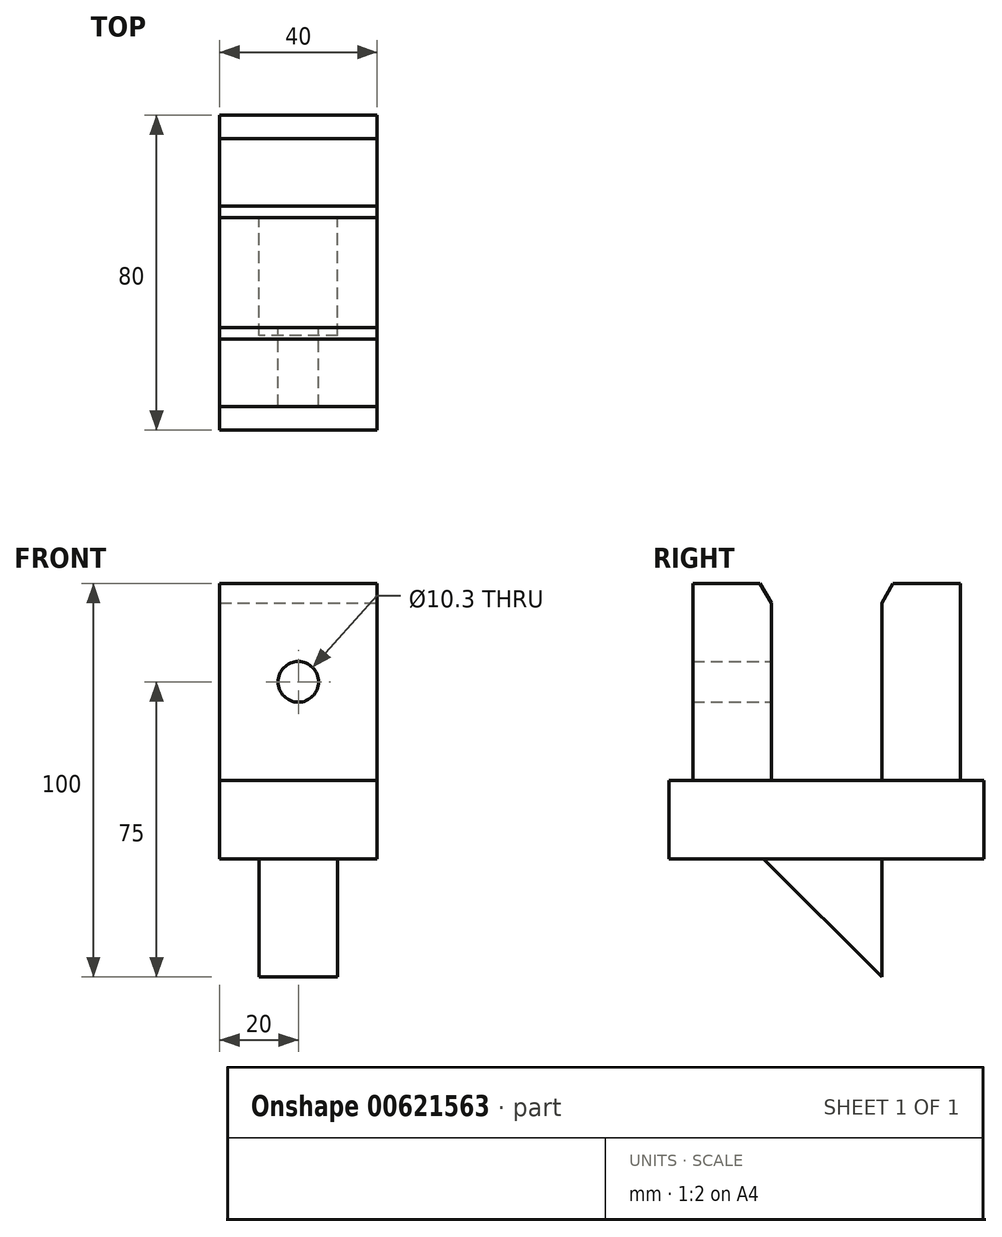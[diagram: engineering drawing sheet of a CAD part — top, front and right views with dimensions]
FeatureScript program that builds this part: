
annotation { "Feature Type Name" : "Feature", "Feature Type Description" : "" }
export const myFeature = defineFeature(function(context is Context, id is Id, definition is map)
    precondition{}
    {
        {
            var Q0;
            Q0=qCreatedBy(makeId("Top.planeOp"),FACE);
            var sketch = newSketch(context, id + "F0", { "sketchPlane" : qUnion([Q0])});
            skLineSegment(sketch, "E0.bottom", {"start": v(20, -40) * mm, "end": v(-20, -40) * mm});
            skLineSegment(sketch, "E0.top", {"start": v(20, 40) * mm, "end": v(-20, 40) * mm});
            skLineSegment(sketch, "E0.left", {"start": v(20, -40) * mm, "end": v(20, 40) * mm});
            skLineSegment(sketch, "E0.right", {"start": v(-20, -40) * mm, "end": v(-20, 40) * mm});
            skPoint(sketch, "E0.middle", {"position": v(0, 0) * mm});
            skSolve(sketch);
        }
        {
            var Q0;
            Q0 = qSketchRegion(id + "F0", true);
            extrude(context, id + "F1", {"entities" : qUnion([Q0]), "depth" : 20 * mm, "offsetDistance" : 25 * mm});
        }
        {
            var Q0;
            Q0=makeQuery(id+"F1.opExtrude","CAP_FACE",FACE,{"disambiguationData":[OSD([sQuery(id+"F0.wireOp",EDGE,"E0.bottom"),sQuery(id+"F0.wireOp",EDGE,"E0.top"),sQuery(id+"F0.wireOp",EDGE,"E0.left"),sQuery(id+"F0.wireOp",EDGE,"E0.right")])],"isStart":false});
            var sketch = newSketch(context, id + "F2", { "sketchPlane" : qUnion([Q0])});
            skLineSegment(sketch, "E1.bottom", {"start": v(20, -34) * mm, "end": v(-20, -34) * mm});
            skLineSegment(sketch, "E1.top", {"start": v(20, -14) * mm, "end": v(-20, -14) * mm});
            skLineSegment(sketch, "E1.left", {"start": v(20, -34) * mm, "end": v(20, -14) * mm});
            skLineSegment(sketch, "E1.right", {"start": v(-20, -34) * mm, "end": v(-20, -14) * mm});
            skPoint(sketch, "E1.middle", {"position": v(0, -24) * mm});
            skLineSegment(sketch, "E2.bottom", {"start": v(-20, 14) * mm, "end": v(20, 14) * mm});
            skLineSegment(sketch, "E2.top", {"start": v(-20, 34) * mm, "end": v(20, 34) * mm});
            skLineSegment(sketch, "E2.left", {"start": v(-20, 14) * mm, "end": v(-20, 34) * mm});
            skLineSegment(sketch, "E2.right", {"start": v(20, 14) * mm, "end": v(20, 34) * mm});
            skPoint(sketch, "E2.middle", {"position": v(0, 24) * mm});
            skSolve(sketch);
        }
        {
            var Q0;
            Q0 = qSketchRegion(id + "F2", true);
            extrude(context, id + "F3", {"entities" : qUnion([Q0]), "depth" : 50 * mm, "offsetDistance" : 25 * mm});
        }
        {
            var Q0;
            Q0=qCreatedBy(makeId("Right.planeOp"),FACE);
            var sketch = newSketch(context, id + "F4", { "sketchPlane" : qUnion([Q0])});
            skLineSegment(sketch, "E3", {"start": v(14, 0) * mm, "end": v(14, -30) * mm});
            skLineSegment(sketch, "E4", {"start": v(14, -30) * mm, "end": v(-16, 0) * mm});
            skLineSegment(sketch, "E5", {"start": v(-16, 0) * mm, "end": v(14, 0) * mm});
            skSolve(sketch);
        }
        {
            var Q0;
            Q0 = qSketchRegion(id + "F4", true);
            extrude(context, id + "F5", {"entities" : qUnion([Q0]), "depth" : 20 * mm, "offsetDistance" : 25 * mm, "symmetric" : true});
        }
        {
            var Q0;
            Q0=makeQuery(id+"F3.opExtrude","SWEPT_FACE",FACE,{"disambiguationData":[OSD([sQuery(id+"F2.wireOp",EDGE,"E1.bottom")])]});
            var sketch = newSketch(context, id + "F6", { "sketchPlane" : qUnion([Q0])});
            skPoint(sketch, "E6", {"position": v(0, 45) * mm});
            skSolve(sketch);
        }
        {
            var Q0;
            Q0=sQuery(id+"F6.wireOp",VERTEX,"E6");
            var Q1;
            Q1=makeQuery(id+"F3.opExtrude","SWEPT_BODY",BODY,{"disambiguationData":[OSD([sQuery(id+"F2.wireOp",EDGE,"E1.bottom"),sQuery(id+"F2.wireOp",EDGE,"E1.top"),sQuery(id+"F2.wireOp",EDGE,"E1.left"),sQuery(id+"F2.wireOp",EDGE,"E1.right")])]});
            hole(context, id + "F7", {"style" : HoleStyle.SIMPLE, "endStyle" : HoleEndStyle.BLIND, "standardTappedOrClearance" : lookupTablePath({ "standard" : "ISO", "engagement" : "75%", "pitch" : "1.75 mm", "size" : "M12", "type" : "Tapped" }), "standardBlindInLast" : lookupTablePath({ "standard" : "ISO", "engagement" : "75%", "pitch" : "1.75 mm", "size" : "M12", "type" : "Tapped" }), "holeDiameter" : 10.3 * mm, "majorDiameter" : 12 * mm, "showTappedDepth" : true, "holeDepth" : 26.5 * mm, "isTappedThrough" : true, "tappedDepth" : 21.25 * mm, "tapClearance" : 3, "startFromSketch" : true, "locations" : qUnion([Q0]), "scope" : qUnion([Q1])});
        }
        {
            var Q0;
            Q0=makeQuery(id+"F3.opExtrude","CAP_EDGE",EDGE,{"disambiguationData":[OSD([sQuery(id+"F2.wireOp",EDGE,"E2.bottom")])],"isStart":false});
            chamfer(context, id + "F8", {"entities" : qUnion([Q0]), "chamferType" : ChamferType.OFFSET_ANGLE, "width" : 5 * mm, "oppositeDirection" : true, "angle" : 30 * degree, "tangentPropagation" : true});
        }
        {
            var Q0;
            Q0=makeQuery(id+"F3.opExtrude","CAP_EDGE",EDGE,{"disambiguationData":[OSD([sQuery(id+"F2.wireOp",EDGE,"E1.top")])],"isStart":false});
            chamfer(context, id + "F9", {"entities" : qUnion([Q0]), "chamferType" : ChamferType.OFFSET_ANGLE, "width" : 5 * mm, "oppositeDirection" : true, "angle" : 30 * degree, "tangentPropagation" : true});
        }
    });
